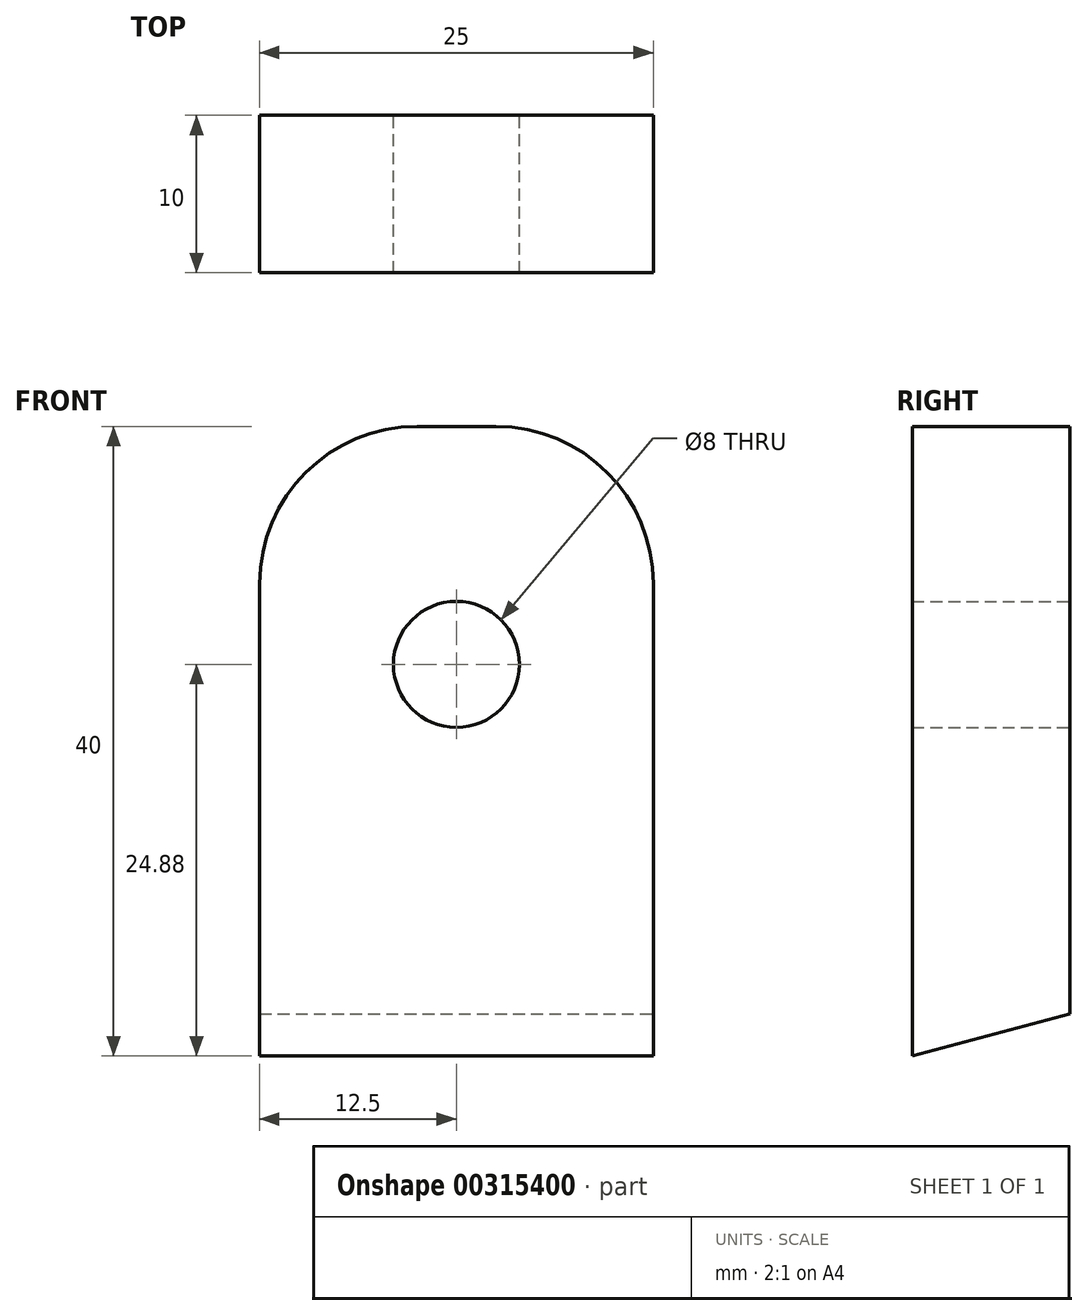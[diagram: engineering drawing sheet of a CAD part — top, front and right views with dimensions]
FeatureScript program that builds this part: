
annotation { "Feature Type Name" : "Feature", "Feature Type Description" : "" }
export const myFeature = defineFeature(function(context is Context, id is Id, definition is map)
    precondition{}
    {
        {
            var Q0;
            Q0=qCreatedBy(makeId("Front.planeOp"),FACE);
            var sketch = newSketch(context, id + "F0", { "sketchPlane" : qUnion([Q0])});
            skPoint(sketch, "E0.middle", {"position": v(0, 0) * mm});
            skCircle(sketch, "E1", {"center": v(0, 0) * mm, "radius": 4 * mm});
            skLineSegment(sketch, "E2.bottom", {"start": v(-12.5, 15.12) * mm, "end": v(12.5, 15.12) * mm});
            skLineSegment(sketch, "E2.top", {"start": v(-12.5, -24.88) * mm, "end": v(12.5, -24.88) * mm});
            skLineSegment(sketch, "E2.left", {"start": v(-12.5, 15.12) * mm, "end": v(-12.5, -24.88) * mm});
            skLineSegment(sketch, "E2.right", {"start": v(12.5, 15.12) * mm, "end": v(12.5, -24.88) * mm});
            skLineSegment(sketch, "E3", {"start": v(0, 0) * mm, "end": v(0, 15.12) * mm, "construction": true});
            skSolve(sketch);
        }
        {
            var Q0;
            Q0=makeQuery(id+"F0.imprint","IMPRINT",FACE,{"disambiguationData":[TD([[makeQuery(id+"F0.imprint","IMPRINT",EDGE,{"derivedFrom":sQuery(id+"F0.wireOp",EDGE,"E1")}),-1.0]])]});
            extrude(context, id + "F1", {"entities" : qUnion([Q0]), "depth" : 10 * mm});
        }
        {
            var Q0;
            Q0=makeQuery(id+"F1.opExtrude","SWEPT_FACE",FACE,{"disambiguationData":[OSD([sQuery(id+"F0.wireOp",EDGE,"E2.right")])]});
            var sketch = newSketch(context, id + "F2", { "sketchPlane" : qUnion([Q0])});
            skLineSegment(sketch, "E4.0.0", {"start": v(0, -24.88) * mm, "end": v(0, 15.12) * mm});
            skLineSegment(sketch, "E4.0.1", {"start": v(0, 15.12) * mm, "end": v(-10, 15.12) * mm});
            skLineSegment(sketch, "E4.0.2", {"start": v(-10, 15.12) * mm, "end": v(-10, -24.88) * mm});
            skLineSegment(sketch, "E4.0.3", {"start": v(-10, -24.88) * mm, "end": v(0, -24.88) * mm});
            skLineSegment(sketch, "E5", {"start": v(-10, -24.88) * mm, "end": v(0, -22.2) * mm});
            skSolve(sketch);
        }
        {
            var Q0;
            {var subQ0=sQuery(id+"F2.wireOp",EDGE,"E4.0.3");Q0=makeQuery(id+"F2.imprint","IMPRINT",FACE,{"disambiguationData":[TD([[makeQuery(id+"F2.imprint","IMPRINT",EDGE,{"derivedFrom":subQ0}),1.0]])]});}
            extrude(context, id + "F3", {"entities" : qUnion([Q0]), "operationType" : NewBodyOperationType.REMOVE, "endBound" : BoundingType.THROUGH_ALL, "oppositeDirection" : true, "depth" : 25 * mm});
        }
        {
            var Q0;
            Q0=makeQuery(id+"F1.opExtrude","SWEPT_EDGE",EDGE,{"disambiguationData":[OSD([sQuery(id+"F0.wireOp",EDGE,"E2.bottom"),sQuery(id+"F0.wireOp",EDGE,"E2.right")])]});
            var Q1;
            Q1=makeQuery(id+"F1.opExtrude","SWEPT_EDGE",EDGE,{"disambiguationData":[OSD([sQuery(id+"F0.wireOp",EDGE,"E2.bottom"),sQuery(id+"F0.wireOp",EDGE,"E2.left")])]});
            fillet(context, id + "F4", {"entities" : qUnion([Q0, Q1]), "radius" : 10 * mm, "tangentPropagation" : true, "allowEdgeOverflow" : false});
        }
    });
